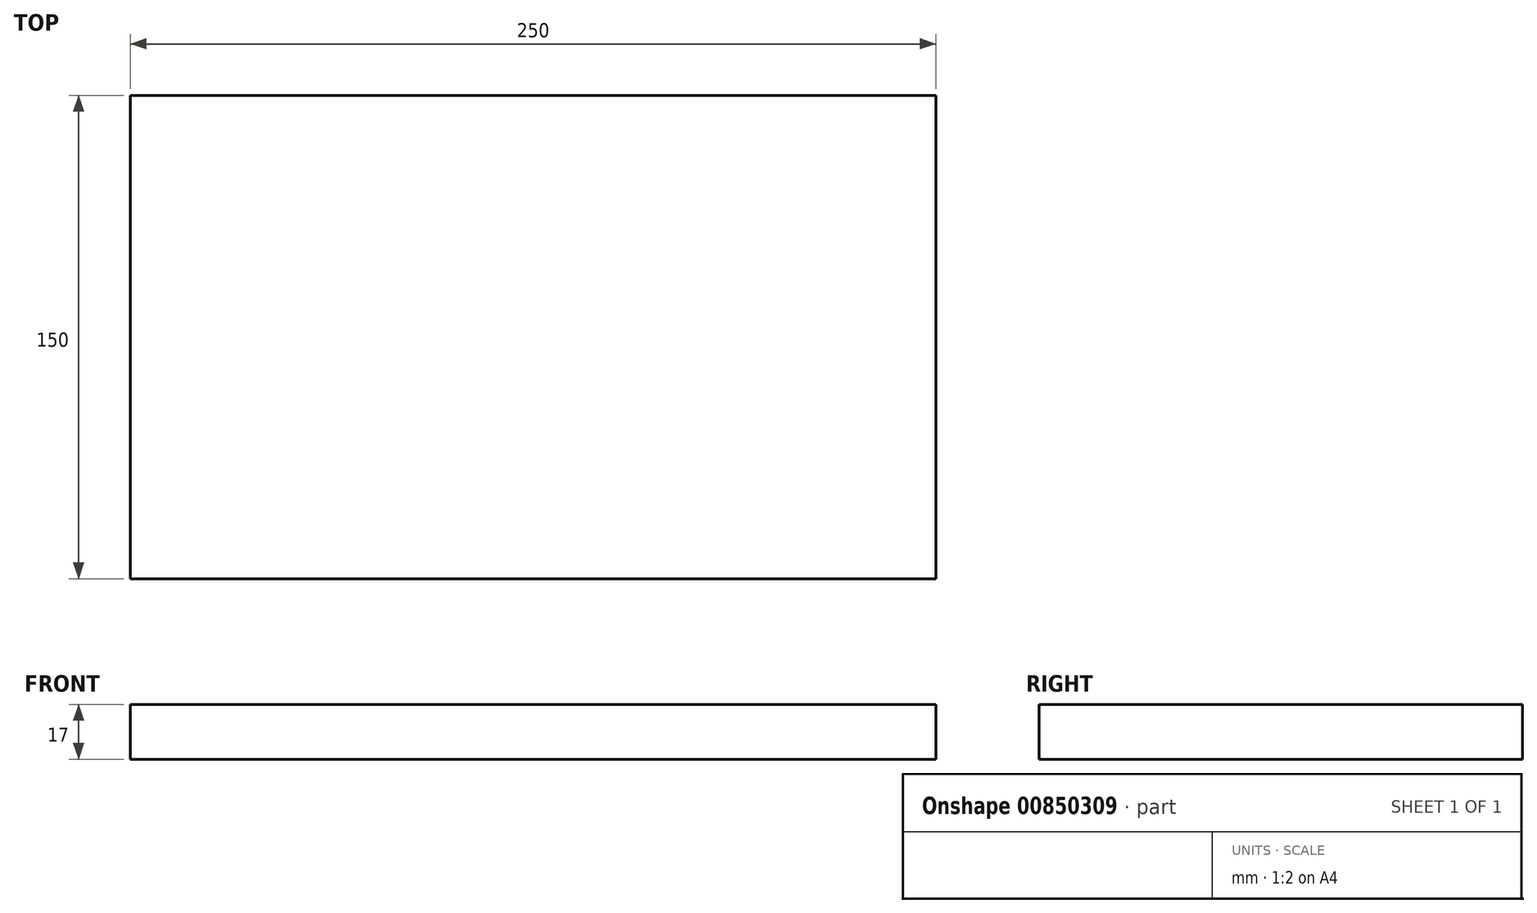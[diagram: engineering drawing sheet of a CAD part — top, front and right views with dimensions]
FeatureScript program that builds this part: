
annotation { "Feature Type Name" : "Feature", "Feature Type Description" : "" }
export const myFeature = defineFeature(function(context is Context, id is Id, definition is map)
    precondition{}
    {
        {
            var Q0;
            Q0=qCreatedBy(makeId("Front.planeOp"),FACE);
            var sketch = newSketch(context, id + "F0", { "sketchPlane" : qUnion([Q0])});
            skLineSegment(sketch, "E0.bottom", {"start": v(250, 145.96) * mm, "end": v(0, 145.96) * mm});
            skLineSegment(sketch, "E0.top", {"start": v(250, 128.96) * mm, "end": v(0, 128.96) * mm});
            skLineSegment(sketch, "E0.left", {"start": v(250, 145.96) * mm, "end": v(250, 128.96) * mm});
            skLineSegment(sketch, "E0.right", {"start": v(0, 145.96) * mm, "end": v(0, 128.96) * mm});
            skSolve(sketch);
        }
        {
            var Q0;
            Q0 = qSketchRegion(id + "F0", true);
            extrude(context, id + "F1", {"entities" : qUnion([Q0]), "oppositeDirection" : true, "depth" : 150 * mm, "offsetDistance" : 25 * mm});
        }
    });
